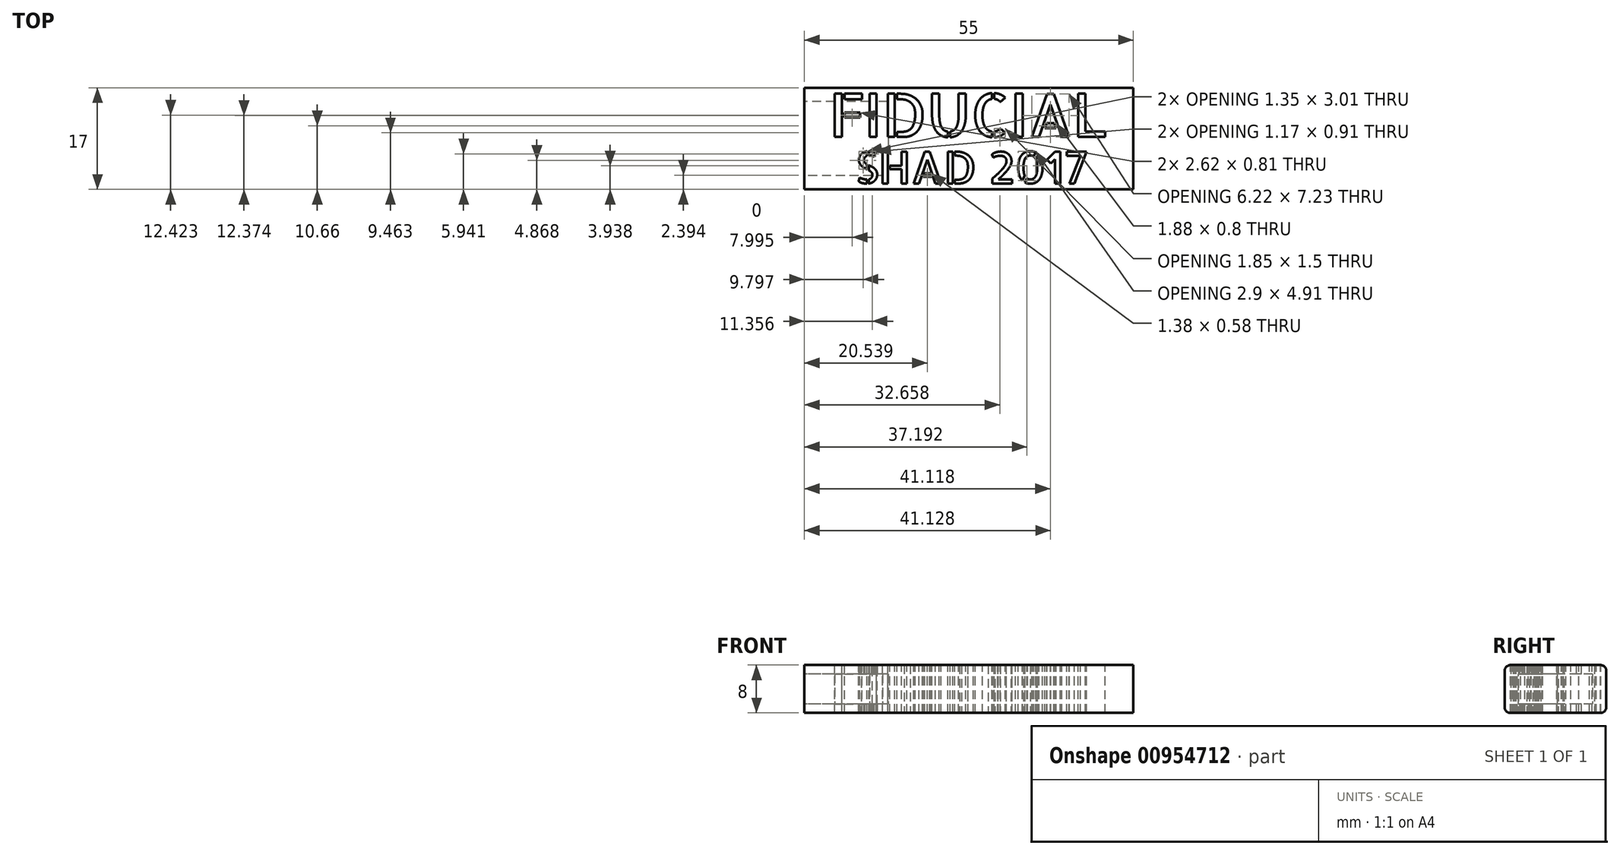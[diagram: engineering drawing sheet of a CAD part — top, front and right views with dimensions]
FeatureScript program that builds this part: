
annotation { "Feature Type Name" : "Feature", "Feature Type Description" : "" }
export const myFeature = defineFeature(function(context is Context, id is Id, definition is map)
    precondition{}
    {
        {
            var Q0;
            Q0=qCreatedBy(makeId("Front.planeOp"),FACE);
            var sketch = newSketch(context, id + "F0", { "sketchPlane" : qUnion([Q0])});
            skLineSegment(sketch, "E0.bottom", {"start": v(76.77, 74) * mm, "end": v(-76.77, 74) * mm});
            skLineSegment(sketch, "E0.top", {"start": v(76.77, -74) * mm, "end": v(-76.77, -74) * mm});
            skLineSegment(sketch, "E0.left", {"start": v(76.77, 74) * mm, "end": v(76.77, -74) * mm});
            skLineSegment(sketch, "E0.right", {"start": v(-76.77, 74) * mm, "end": v(-76.77, -74) * mm});
            skPoint(sketch, "E0.middle", {"position": v(0, 0) * mm});
            skSolve(sketch);
        }
        {
            var Q0;
            Q0=makeQuery(id+"F0.imprint","IMPRINT",FACE,{"disambiguationData":[TD([[makeQuery(id+"F0.imprint","IMPRINT",EDGE,{"derivedFrom":sQuery(id+"F0.wireOp",EDGE,"E0.bottom")}),1.0]])]});
            var sketch = newSketch(context, id + "F1", { "sketchPlane" : qUnion([Q0])});
            skLineSegment(sketch, "E1.bottom", {"start": v(-7.5, 4) * mm, "end": v(7.5, 4) * mm});
            skLineSegment(sketch, "E1.top", {"start": v(-7.5, -4) * mm, "end": v(7.5, -4) * mm});
            skLineSegment(sketch, "E1.left", {"start": v(-8.5, 3) * mm, "end": v(-8.5, -3) * mm});
            skLineSegment(sketch, "E1.right", {"start": v(8.5, 3) * mm, "end": v(8.5, -3) * mm});
            skPoint(sketch, "E1.middle", {"position": v(0, 0) * mm});
            skPoint(sketch, "E2.visualSharp", {"position": v(-8.5, 4) * mm});
            skArc(sketch, "E2.filletArc", {"start": v(-7.5, 4) * mm, "mid": v(-8.2, 3.7) * mm, "end": v(-8.5, 3) * mm});
            skPoint(sketch, "E3.visualSharp", {"position": v(-8.5, -4) * mm});
            skArc(sketch, "E3.filletArc", {"start": v(-8.5, -3) * mm, "mid": v(-8.2, -3.7) * mm, "end": v(-7.5, -4) * mm});
            skPoint(sketch, "E4.visualSharp", {"position": v(8.5, 4) * mm});
            skArc(sketch, "E4.filletArc", {"start": v(8.5, 3) * mm, "mid": v(8.2, 3.7) * mm, "end": v(7.5, 4) * mm});
            skPoint(sketch, "E5.visualSharp", {"position": v(8.5, -4) * mm});
            skArc(sketch, "E5.filletArc", {"start": v(7.5, -4) * mm, "mid": v(8.2, -3.7) * mm, "end": v(8.5, -3) * mm});
            skSolve(sketch);
        }
        {
            var Q0;
            Q0=qSketchRegion(id+"F1",true);
            extrude(context, id + "F2", {"entities" : qUnion([Q0]), "depth" : 55 * mm, "offsetDistance" : 25 * mm});
        }
        {
            var Q0;
            Q0=makeQuery(id+"F2.opExtrude","CAP_FACE",FACE,{"disambiguationData":[OSD([sQuery(id+"F1.wireOp",EDGE,"E1.bottom"),sQuery(id+"F1.wireOp",EDGE,"E1.top"),sQuery(id+"F1.wireOp",EDGE,"E1.left"),sQuery(id+"F1.wireOp",EDGE,"E1.right"),sQuery(id+"F1.wireOp",EDGE,"E2.filletArc"),sQuery(id+"F1.wireOp",EDGE,"E3.filletArc"),sQuery(id+"F1.wireOp",EDGE,"E4.filletArc"),sQuery(id+"F1.wireOp",EDGE,"E5.filletArc")])],"isStart":false});
            var sketch = newSketch(context, id + "F3", { "sketchPlane" : qUnion([Q0])});
            skLineSegment(sketch, "E6.bottom", {"start": v(-6.2, 2.5) * mm, "end": v(6.2, 2.5) * mm});
            skLineSegment(sketch, "E6.top", {"start": v(-6.2, -2.5) * mm, "end": v(6.2, -2.5) * mm});
            skLineSegment(sketch, "E6.left", {"start": v(-6.2, 2.5) * mm, "end": v(-6.2, -2.5) * mm});
            skLineSegment(sketch, "E6.right", {"start": v(6.2, 2.5) * mm, "end": v(6.2, -2.5) * mm});
            skPoint(sketch, "E6.middle", {"position": v(0, 0) * mm});
            skSolve(sketch);
        }
        {
            var Q0;
            Q0=makeQuery(id+"F3.imprint","IMPRINT",FACE,{"disambiguationData":[TD([[makeQuery(id+"F3.imprint","IMPRINT",EDGE,{"derivedFrom":sQuery(id+"F3.wireOp",EDGE,"E6.bottom")}),-1.0]])]});
            extrude(context, id + "F4", {"entities" : qUnion([Q0]), "operationType" : NewBodyOperationType.REMOVE, "oppositeDirection" : true, "depth" : 14 * mm, "offsetDistance" : 25 * mm});
        }
        {
            var Q0;
            Q0=makeQuery(id+"F2.opExtrude","SWEPT_FACE",FACE,{"disambiguationData":[OSD([sQuery(id+"F1.wireOp",EDGE,"E1.bottom")])]});
            var sketch = newSketch(context, id + "F5", { "sketchPlane" : qUnion([Q0])});
            skSolve(sketch);
        }
        {
            var Q0;
            Q0=makeQuery(id+"F2.opExtrude","SWEPT_BODY",BODY,{"disambiguationData":[OSD([sQuery(id+"F1.wireOp",EDGE,"E1.bottom"),sQuery(id+"F1.wireOp",EDGE,"E1.top"),sQuery(id+"F1.wireOp",EDGE,"E1.left"),sQuery(id+"F1.wireOp",EDGE,"E1.right"),sQuery(id+"F1.wireOp",EDGE,"E2.filletArc"),sQuery(id+"F1.wireOp",EDGE,"E3.filletArc"),sQuery(id+"F1.wireOp",EDGE,"E4.filletArc"),sQuery(id+"F1.wireOp",EDGE,"E5.filletArc")])]});
            var Q1;
            Q1=makeQuery(id+"F2.opExtrude","CAP_EDGE",EDGE,{"disambiguationData":[OSD([sQuery(id+"F1.wireOp",EDGE,"E1.left")])],"isStart":false});
            transform(context, id + "F6", {"entities" : qUnion([Q0]), "transformType" : TransformType.ROTATION, "transformAxis" : qUnion([Q1]), "angle" : 90 * degree, "makeCopy" : false});
        }
        {
            var Q0;
            Q0=makeQuery(id+"F2.opExtrude","SWEPT_FACE",FACE,{"disambiguationData":[OSD([sQuery(id+"F1.wireOp",EDGE,"E1.bottom")])]});
            var sketch = newSketch(context, id + "F7", { "sketchPlane" : qUnion([Q0])});
            skText(sketch, "E7", { "text": "FIDUCIAL", "fontName": "AllertaStencil-Regular.ttf"});
            skText(sketch, "E8", { "text": "SHAD 2017", "fontName": "AllertaStencil-Regular.ttf"});
            const initialGuessF7  = {"E7": [-0.00435, -0.06324, 1, 0, 0.00724], "E8": [0, -0.071, 1, 0, 0.00531]};
            skSetInitialGuess(sketch, initialGuessF7);
            skSolve(sketch);
        }
        {
            var Q0;
            Q0 = qSketchRegion(id + "F7", true);
            extrude(context, id + "F8", {"entities" : qUnion([Q0]), "operationType" : NewBodyOperationType.REMOVE, "endBound" : BoundingType.THROUGH_ALL, "oppositeDirection" : true, "depth" : 25 * mm, "offsetDistance" : 25 * mm});
        }
    });
